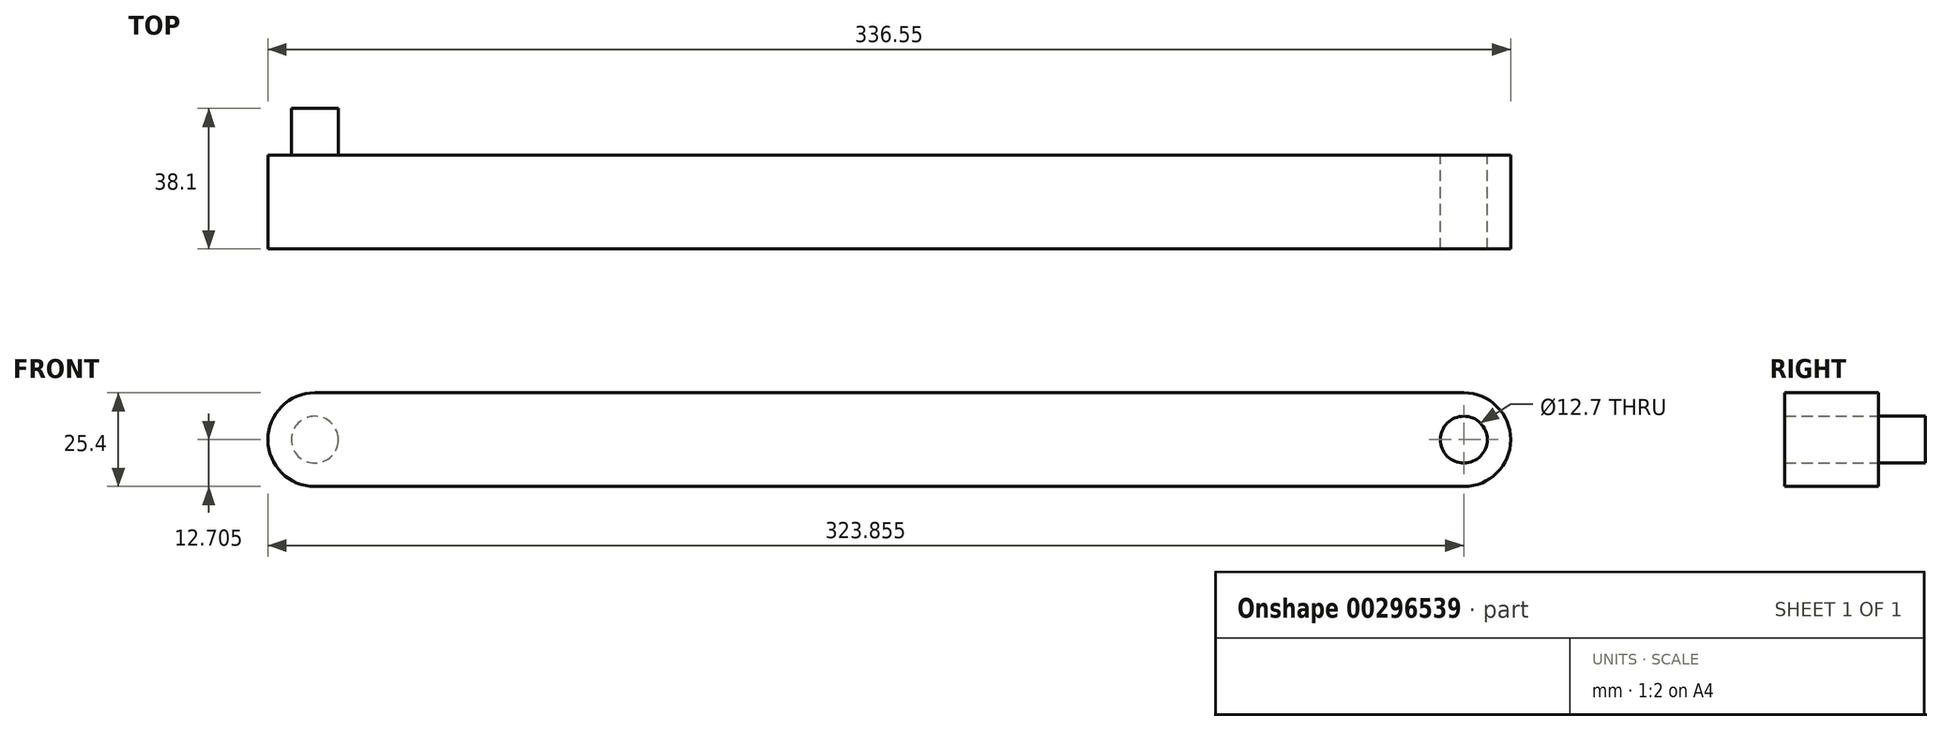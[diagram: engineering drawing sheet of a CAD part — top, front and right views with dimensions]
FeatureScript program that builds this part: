
annotation { "Feature Type Name" : "Feature", "Feature Type Description" : "" }
export const myFeature = defineFeature(function(context is Context, id is Id, definition is map)
    precondition{}
    {
        {
            var Q0;
            Q0=qCreatedBy(makeId("Front.planeOp"),FACE);
            var sketch = newSketch(context, id + "F0", { "sketchPlane" : qUnion([Q0])});
            skLineSegment(sketch, "E0.bottom", {"start": v(-138.82, -4.13) * mm, "end": v(197.73, -4.13) * mm});
            skLineSegment(sketch, "E0.top", {"start": v(-138.82, -29.53) * mm, "end": v(197.73, -29.53) * mm});
            skLineSegment(sketch, "E0.left", {"start": v(-138.82, -4.13) * mm, "end": v(-138.82, -29.53) * mm});
            skLineSegment(sketch, "E0.right", {"start": v(197.73, -4.13) * mm, "end": v(197.73, -29.53) * mm});
            skSolve(sketch);
        }
        {
            var Q0;
            Q0=makeQuery(id+"F0.imprint","IMPRINT",FACE,{"disambiguationData":[TD([[makeQuery(id+"F0.imprint","IMPRINT",EDGE,{"derivedFrom":sQuery(id+"F0.wireOp",EDGE,"E0.bottom")}),-1.0]])]});
            extrude(context, id + "F1", {"entities" : qUnion([Q0]), "depth" : 25.4 * mm});
        }
        {
            var Q0;
            Q0=makeQuery(id+"F1.opExtrude","SWEPT_EDGE",EDGE,{"disambiguationData":[OSD([sQuery(id+"F0.wireOp",EDGE,"E0.bottom"),sQuery(id+"F0.wireOp",EDGE,"E0.left")])]});
            var Q1;
            Q1=makeQuery(id+"F1.opExtrude","SWEPT_EDGE",EDGE,{"disambiguationData":[OSD([sQuery(id+"F0.wireOp",EDGE,"E0.top"),sQuery(id+"F0.wireOp",EDGE,"E0.left")])]});
            var Q2;
            Q2=makeQuery(id+"F1.opExtrude","SWEPT_EDGE",EDGE,{"disambiguationData":[OSD([sQuery(id+"F0.wireOp",EDGE,"E0.top"),sQuery(id+"F0.wireOp",EDGE,"E0.right")])]});
            var Q3;
            Q3=makeQuery(id+"F1.opExtrude","SWEPT_EDGE",EDGE,{"disambiguationData":[OSD([sQuery(id+"F0.wireOp",EDGE,"E0.bottom"),sQuery(id+"F0.wireOp",EDGE,"E0.right")])]});
            fillet(context, id + "F2", {"entities" : qUnion([Q0, Q1, Q2, Q3]), "radius" : 12.7 * mm, "tangentPropagation" : true, "allowEdgeOverflow" : false});
        }
        {
            var Q0;
            Q0=makeQuery(id+"F1.opExtrude","CAP_FACE",FACE,{"disambiguationData":[OSD([sQuery(id+"F0.wireOp",EDGE,"E0.bottom"),sQuery(id+"F0.wireOp",EDGE,"E0.top"),sQuery(id+"F0.wireOp",EDGE,"E0.left"),sQuery(id+"F0.wireOp",EDGE,"E0.right")])],"isStart":true});
            var sketch = newSketch(context, id + "F3", { "sketchPlane" : qUnion([Q0])});
            skCircle(sketch, "E1", {"center": v(126.12, -16.83) * mm, "radius": 6.35 * mm});
            skSolve(sketch);
        }
        {
            var Q0;
            Q0=makeQuery(id+"F3.imprint","IMPRINT",FACE,{"disambiguationData":[TD([[makeQuery(id+"F3.imprint","IMPRINT",EDGE,{"derivedFrom":sQuery(id+"F3.wireOp",EDGE,"E1")}),1.0]])]});
            extrude(context, id + "F4", {"entities" : qUnion([Q0]), "operationType" : NewBodyOperationType.ADD, "depth" : 12.7 * mm});
        }
        {
            var Q0;
            Q0=makeQuery(id+"F1.opExtrude","CAP_FACE",FACE,{"disambiguationData":[OSD([sQuery(id+"F0.wireOp",EDGE,"E0.bottom"),sQuery(id+"F0.wireOp",EDGE,"E0.top"),sQuery(id+"F0.wireOp",EDGE,"E0.left"),sQuery(id+"F0.wireOp",EDGE,"E0.right")])],"isStart":true});
            var sketch = newSketch(context, id + "F5", { "sketchPlane" : qUnion([Q0])});
            skCircle(sketch, "E2", {"center": v(-185.03, -16.83) * mm, "radius": 6.35 * mm});
            skSolve(sketch);
        }
        {
            var Q0;
            Q0=makeQuery(id+"F5.imprint","IMPRINT",FACE,{"disambiguationData":[TD([[makeQuery(id+"F5.imprint","IMPRINT",EDGE,{"derivedFrom":sQuery(id+"F5.wireOp",EDGE,"E2")}),1.0]])]});
            extrude(context, id + "F6", {"entities" : qUnion([Q0]), "operationType" : NewBodyOperationType.REMOVE, "endBound" : BoundingType.THROUGH_ALL, "oppositeDirection" : true, "depth" : 25.4 * mm});
        }
    });
